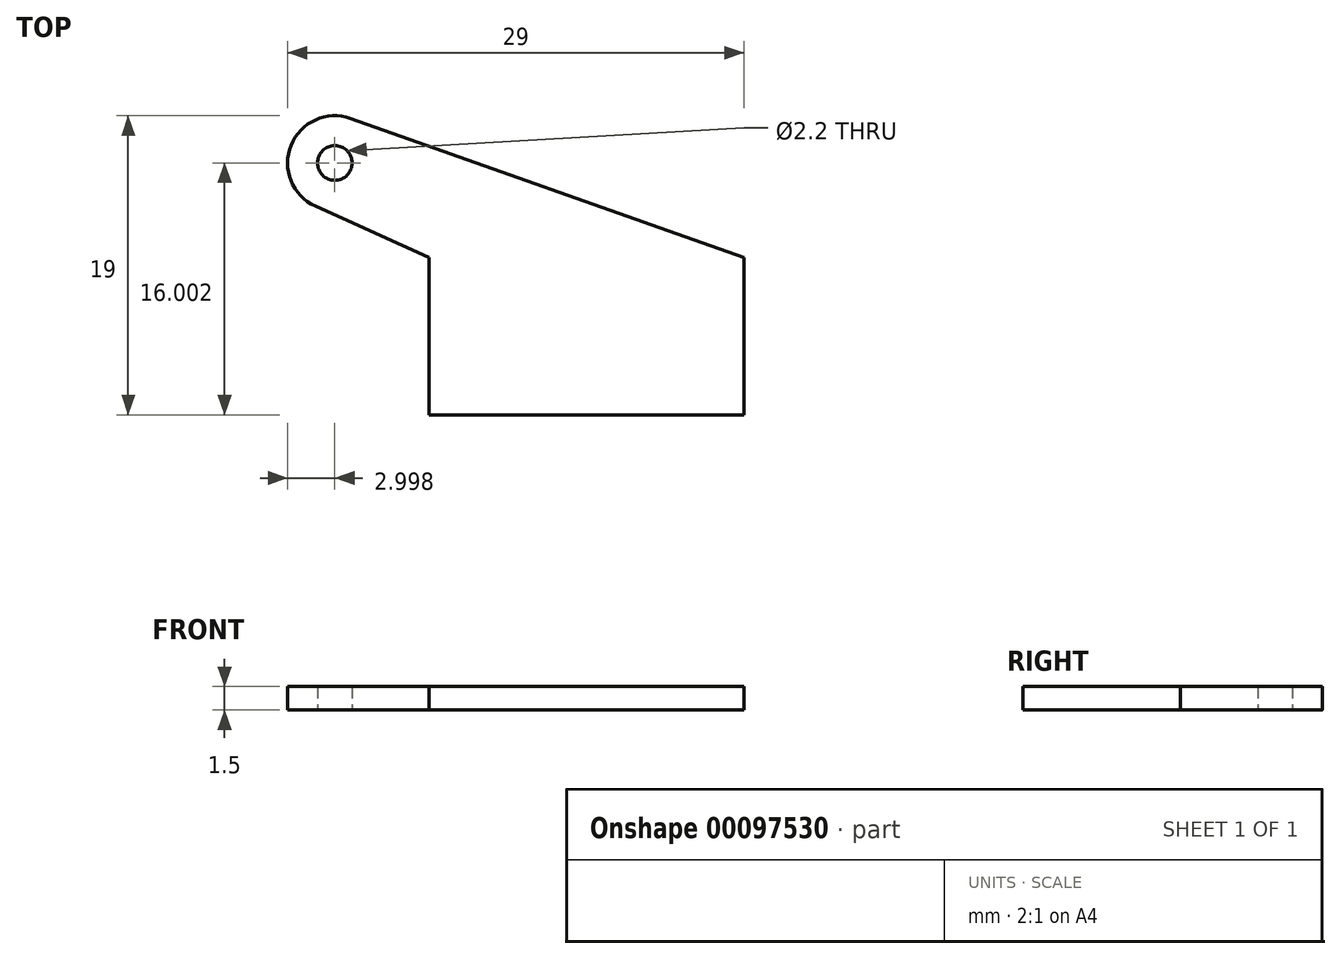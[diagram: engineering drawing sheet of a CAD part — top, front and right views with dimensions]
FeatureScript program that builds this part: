
annotation { "Feature Type Name" : "Feature", "Feature Type Description" : "" }
export const myFeature = defineFeature(function(context is Context, id is Id, definition is map)
    precondition{}
    {
        {
            var Q0;
            Q0=qCreatedBy(makeId("Top.planeOp"),FACE);
            var sketch = newSketch(context, id + "F0", { "sketchPlane" : qUnion([Q0])});
            skLineSegment(sketch, "E0.top", {"start": v(-8.78, -13.78) * mm, "end": v(11.22, -13.78) * mm});
            skLineSegment(sketch, "E0.left", {"start": v(-8.78, -3.78) * mm, "end": v(-8.78, -13.78) * mm});
            skLineSegment(sketch, "E0.right", {"start": v(11.22, -3.78) * mm, "end": v(11.22, -13.78) * mm});
            skLineSegment(sketch, "E1", {"start": v(-8.78, -3.78) * mm, "end": v(-17.78, -3.78) * mm, "construction": true});
            skLineSegment(sketch, "E2", {"start": v(-17.78, -3.78) * mm, "end": v(-17.78, 5.22) * mm, "construction": true});
            skLineSegment(sketch, "E3", {"start": v(-17.78, 5.22) * mm, "end": v(-14.78, 5.22) * mm, "construction": true});
            skLineSegment(sketch, "E4", {"start": v(-14.78, 5.22) * mm, "end": v(-14.78, 2.22) * mm, "construction": true});
            skCircle(sketch, "E5", {"center": v(-14.78, 2.22) * mm, "radius": 1.1 * mm});
            skLineSegment(sketch, "E6", {"start": v(-8.78, -3.78) * mm, "end": v(-16.02, -0.51) * mm});
            skPoint(sketch, "E7.orphan", {"position": v(-17.15, 0) * mm});
            skLineSegment(sketch, "E8", {"start": v(11.22, -3.78) * mm, "end": v(-13.78, 5.05) * mm});
            skPoint(sketch, "E9.orphan", {"position": v(-14.27, 5.22) * mm});
            skArc(sketch, "E10", {"start": v(-13.78, 5.05) * mm, "mid": v(-17.57, 3.34) * mm, "end": v(-16.02, -0.51) * mm});
            skSolve(sketch);
        }
        {
            var Q0;
            Q0=makeQuery(id+"F0.imprint","IMPRINT",FACE,{"disambiguationData":[TD([[makeQuery(id+"F0.imprint","IMPRINT",EDGE,{"derivedFrom":sQuery(id+"F0.wireOp",EDGE,"E0.top")}),1.0]])]});
            extrude(context, id + "F1", {"entities" : qUnion([Q0]), "depth" : 1.5 * mm});
        }
    });
